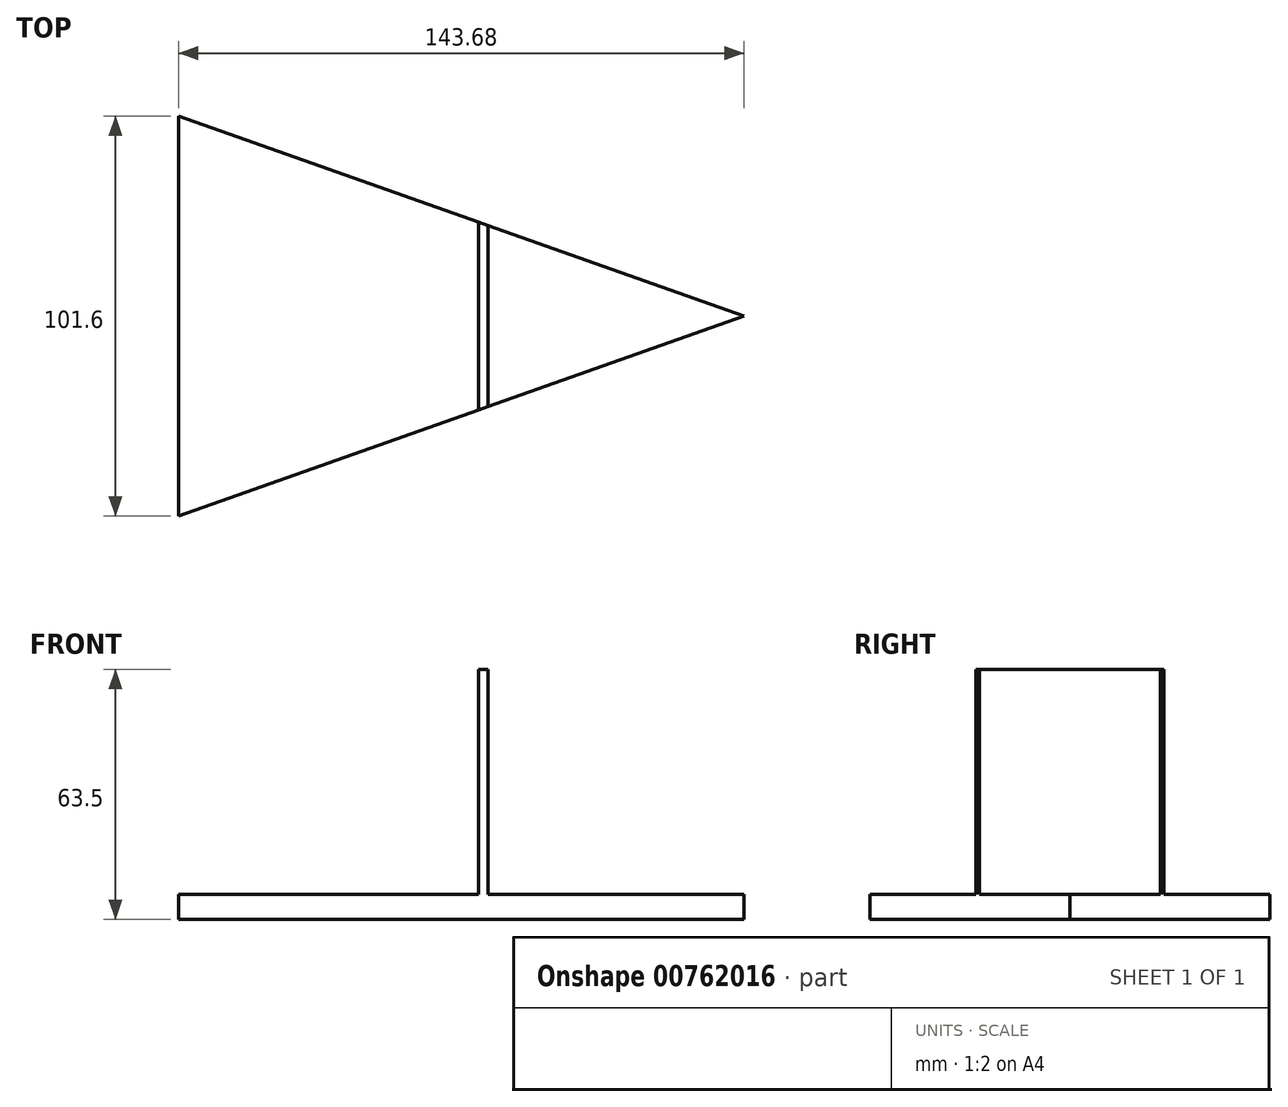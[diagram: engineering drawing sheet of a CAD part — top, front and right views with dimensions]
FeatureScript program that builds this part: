
annotation { "Feature Type Name" : "Feature", "Feature Type Description" : "" }
export const myFeature = defineFeature(function(context is Context, id is Id, definition is map)
    precondition{}
    {
        {
            var Q0;
            Q0=qCreatedBy(makeId("Top.planeOp"),FACE);
            var sketch = newSketch(context, id + "F0", { "sketchPlane" : qUnion([Q0])});
            skLineSegment(sketch, "E0", {"start": v(-82.05, 50.8) * mm, "end": v(-82.05, -50.8) * mm});
            skLineSegment(sketch, "E1", {"start": v(-82.05, 50.8) * mm, "end": v(61.63, 0) * mm});
            skLineSegment(sketch, "E2", {"start": v(-82.05, -50.8) * mm, "end": v(61.63, 0) * mm});
            skLineSegment(sketch, "E3", {"start": v(-5.85, 23.86) * mm, "end": v(-5.85, -23.86) * mm});
            skLineSegment(sketch, "E4", {"start": v(-3.36, 22.98) * mm, "end": v(-3.36, -22.98) * mm});
            skSolve(sketch);
        }
        {
            var Q0;
            {var subQ0=sQuery(id+"F0.wireOp",EDGE,"E3");Q0=makeQuery(id+"F0.imprint","IMPRINT",FACE,{"disambiguationData":[TD([[makeQuery(id+"F0.imprint","IMPRINT",EDGE,{"derivedFrom":subQ0}),1.0]])]});}
            extrude(context, id + "F1", {"entities" : qUnion([Q0]), "depth" : 63.5 * mm, "offsetDistance" : 25.4 * mm});
        }
        {
            var Q0;
            Q0 = qSketchRegion(id + "F0", true);
            extrude(context, id + "F2", {"entities" : qUnion([Q0]), "operationType" : NewBodyOperationType.ADD, "depth" : 6.35 * mm, "offsetDistance" : 25.4 * mm});
        }
    });
